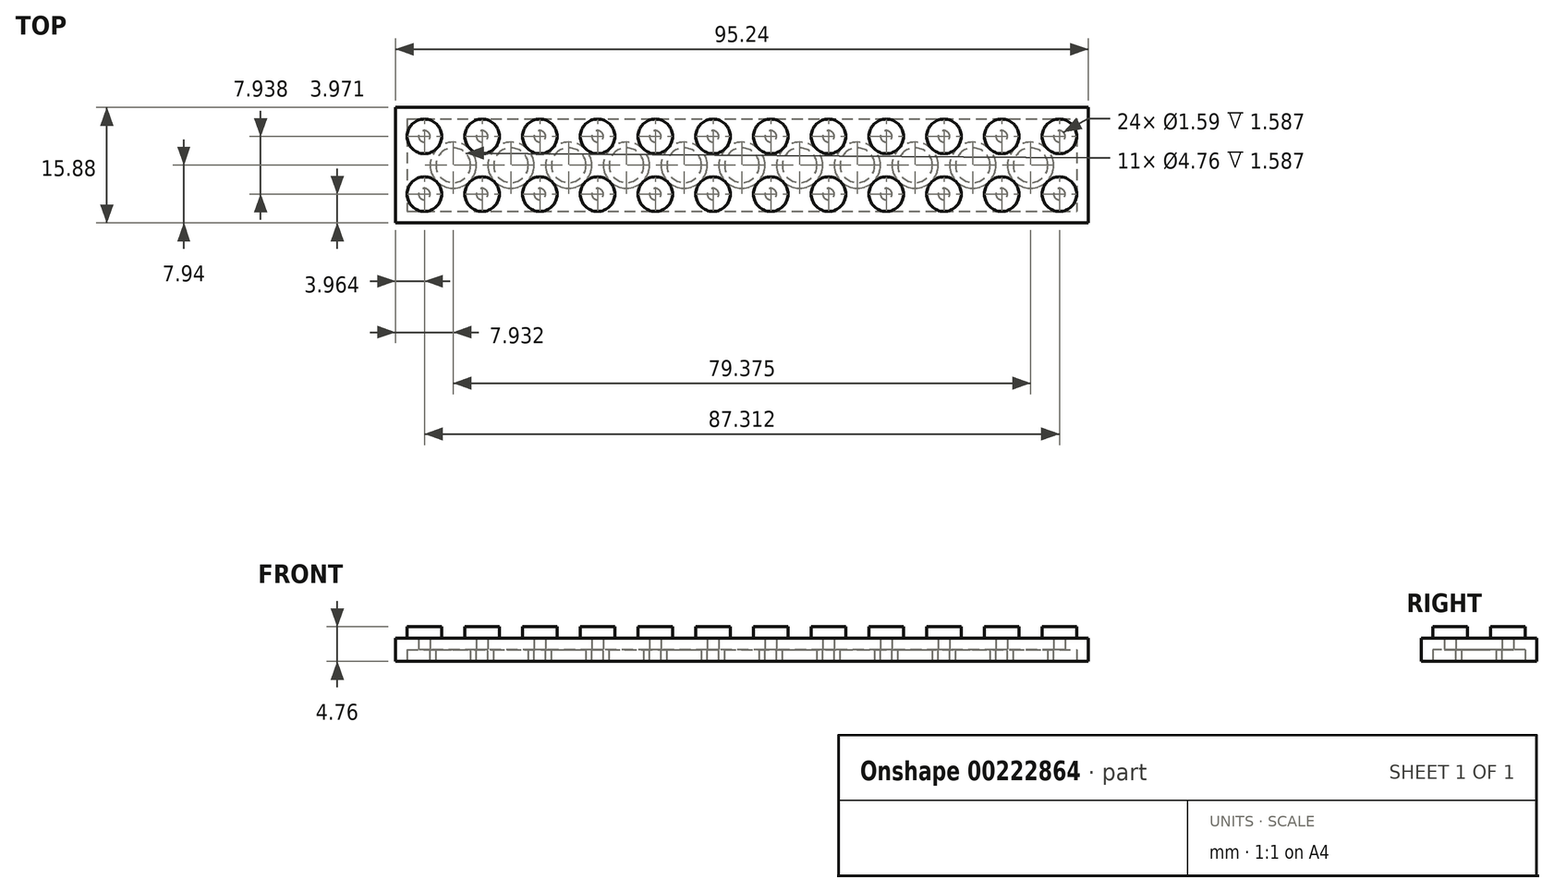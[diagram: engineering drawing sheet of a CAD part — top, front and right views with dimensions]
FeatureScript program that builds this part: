
annotation { "Feature Type Name" : "Feature", "Feature Type Description" : "" }
export const myFeature = defineFeature(function(context is Context, id is Id, definition is map)
    precondition{}
    {
        {
            var Q0;
            Q0=qCreatedBy(makeId("Top.planeOp"),FACE);
            var sketch = newSketch(context, id + "F0", { "sketchPlane" : qUnion([Q0])});
            skLineSegment(sketch, "E0.bottom", {"start": v(-47.63, 7.94) * mm, "end": v(47.63, 7.94) * mm});
            skLineSegment(sketch, "E0.top", {"start": v(-47.63, -7.94) * mm, "end": v(47.63, -7.94) * mm});
            skLineSegment(sketch, "E0.left", {"start": v(-47.63, 7.94) * mm, "end": v(-47.63, -7.94) * mm});
            skLineSegment(sketch, "E0.right", {"start": v(47.63, 7.94) * mm, "end": v(47.63, -7.94) * mm});
            skPoint(sketch, "E0.middle", {"position": v(0, 0) * mm});
            skCircle(sketch, "E1", {"center": v(-43.66, 3.97) * mm, "radius": 2.38 * mm});
            skCircle(sketch, "E2.0.1.0", {"center": v(-43.66, -3.97) * mm, "radius": 2.38 * mm});
            skCircle(sketch, "E2.1.0.0", {"center": v(-35.72, 3.97) * mm, "radius": 2.38 * mm});
            skCircle(sketch, "E2.1.1.0", {"center": v(-35.72, -3.97) * mm, "radius": 2.38 * mm});
            skCircle(sketch, "E2.2.0.0", {"center": v(-27.78, 3.97) * mm, "radius": 2.38 * mm});
            skCircle(sketch, "E2.2.1.0", {"center": v(-27.78, -3.97) * mm, "radius": 2.38 * mm});
            skCircle(sketch, "E2.3.0.0", {"center": v(-19.84, 3.97) * mm, "radius": 2.38 * mm});
            skCircle(sketch, "E2.3.1.0", {"center": v(-19.84, -3.97) * mm, "radius": 2.38 * mm});
            skCircle(sketch, "E2.4.0.0", {"center": v(-11.9, 3.97) * mm, "radius": 2.38 * mm});
            skCircle(sketch, "E2.4.1.0", {"center": v(-11.9, -3.97) * mm, "radius": 2.38 * mm});
            skCircle(sketch, "E2.5.0.0", {"center": v(-3.97, 3.97) * mm, "radius": 2.38 * mm});
            skCircle(sketch, "E2.5.1.0", {"center": v(-3.97, -3.97) * mm, "radius": 2.38 * mm});
            skCircle(sketch, "E2.6.0.0", {"center": v(3.97, 3.97) * mm, "radius": 2.38 * mm});
            skCircle(sketch, "E2.6.1.0", {"center": v(3.97, -3.97) * mm, "radius": 2.38 * mm});
            skCircle(sketch, "E2.7.0.0", {"center": v(11.9, 3.97) * mm, "radius": 2.38 * mm});
            skCircle(sketch, "E2.7.1.0", {"center": v(11.9, -3.97) * mm, "radius": 2.38 * mm});
            skCircle(sketch, "E2.8.0.0", {"center": v(19.84, 3.97) * mm, "radius": 2.38 * mm});
            skCircle(sketch, "E2.8.1.0", {"center": v(19.84, -3.97) * mm, "radius": 2.38 * mm});
            skCircle(sketch, "E2.9.0.0", {"center": v(27.78, 3.97) * mm, "radius": 2.38 * mm});
            skCircle(sketch, "E2.9.1.0", {"center": v(27.78, -3.97) * mm, "radius": 2.38 * mm});
            skCircle(sketch, "E2.10.0.0", {"center": v(35.72, 3.97) * mm, "radius": 2.38 * mm});
            skCircle(sketch, "E2.10.1.0", {"center": v(35.72, -3.97) * mm, "radius": 2.38 * mm});
            skCircle(sketch, "E2.11.0.0", {"center": v(43.66, 3.97) * mm, "radius": 2.38 * mm});
            skCircle(sketch, "E2.11.1.0", {"center": v(43.66, -3.97) * mm, "radius": 2.38 * mm});
            skLineSegment(sketch, "E2.direction1", {"start": v(-43.66, 3.97) * mm, "end": v(-35.72, 3.97) * mm, "construction": true});
            skLineSegment(sketch, "E2.direction2", {"start": v(-43.66, 3.97) * mm, "end": v(-43.66, -3.97) * mm, "construction": true});
            skSolve(sketch);
        }
        {
            var Q0;
            Q0=makeQuery(id+"F0.imprint","IMPRINT",FACE,{"disambiguationData":[TD([[makeQuery(id+"F0.imprint","IMPRINT",EDGE,{"derivedFrom":sQuery(id+"F0.wireOp",EDGE,"E0.bottom")}),-1.0]])]});
            extrude(context, id + "F1", {"entities" : qUnion([Q0]), "depth" : 3.17 * mm});
        }
        {
            var Q0;
            Q0=makeQuery(id+"F0.imprint","IMPRINT",FACE,{"disambiguationData":[TD([[makeQuery(id+"F0.imprint","IMPRINT",EDGE,{"derivedFrom":sQuery(id+"F0.wireOp",EDGE,"E1")}),1.0]])]});
            var Q1;
            Q1=makeQuery(id+"F0.imprint","IMPRINT",FACE,{"disambiguationData":[TD([[makeQuery(id+"F0.imprint","IMPRINT",EDGE,{"derivedFrom":sQuery(id+"F0.wireOp",EDGE,"E2.0.1.0")}),1.0]])]});
            var Q2;
            Q2=makeQuery(id+"F0.imprint","IMPRINT",FACE,{"disambiguationData":[TD([[makeQuery(id+"F0.imprint","IMPRINT",EDGE,{"derivedFrom":sQuery(id+"F0.wireOp",EDGE,"E2.1.1.0")}),1.0]])]});
            var Q3;
            Q3=makeQuery(id+"F0.imprint","IMPRINT",FACE,{"disambiguationData":[TD([[makeQuery(id+"F0.imprint","IMPRINT",EDGE,{"derivedFrom":sQuery(id+"F0.wireOp",EDGE,"E2.1.0.0")}),1.0]])]});
            var Q4;
            Q4=makeQuery(id+"F0.imprint","IMPRINT",FACE,{"disambiguationData":[TD([[makeQuery(id+"F0.imprint","IMPRINT",EDGE,{"derivedFrom":sQuery(id+"F0.wireOp",EDGE,"E2.2.0.0")}),1.0]])]});
            var Q5;
            Q5=makeQuery(id+"F0.imprint","IMPRINT",FACE,{"disambiguationData":[TD([[makeQuery(id+"F0.imprint","IMPRINT",EDGE,{"derivedFrom":sQuery(id+"F0.wireOp",EDGE,"E2.3.1.0")}),1.0]])]});
            var Q6;
            Q6=makeQuery(id+"F0.imprint","IMPRINT",FACE,{"disambiguationData":[TD([[makeQuery(id+"F0.imprint","IMPRINT",EDGE,{"derivedFrom":sQuery(id+"F0.wireOp",EDGE,"E2.3.0.0")}),1.0]])]});
            var Q7;
            Q7=makeQuery(id+"F0.imprint","IMPRINT",FACE,{"disambiguationData":[TD([[makeQuery(id+"F0.imprint","IMPRINT",EDGE,{"derivedFrom":sQuery(id+"F0.wireOp",EDGE,"E2.4.0.0")}),1.0]])]});
            var Q8;
            Q8=makeQuery(id+"F0.imprint","IMPRINT",FACE,{"disambiguationData":[TD([[makeQuery(id+"F0.imprint","IMPRINT",EDGE,{"derivedFrom":sQuery(id+"F0.wireOp",EDGE,"E2.4.1.0")}),1.0]])]});
            var Q9;
            Q9=makeQuery(id+"F0.imprint","IMPRINT",FACE,{"disambiguationData":[TD([[makeQuery(id+"F0.imprint","IMPRINT",EDGE,{"derivedFrom":sQuery(id+"F0.wireOp",EDGE,"E2.2.1.0")}),1.0]])]});
            var Q10;
            Q10=makeQuery(id+"F0.imprint","IMPRINT",FACE,{"disambiguationData":[TD([[makeQuery(id+"F0.imprint","IMPRINT",EDGE,{"derivedFrom":sQuery(id+"F0.wireOp",EDGE,"E2.5.1.0")}),1.0]])]});
            var Q11;
            Q11=makeQuery(id+"F0.imprint","IMPRINT",FACE,{"disambiguationData":[TD([[makeQuery(id+"F0.imprint","IMPRINT",EDGE,{"derivedFrom":sQuery(id+"F0.wireOp",EDGE,"E2.5.0.0")}),1.0]])]});
            var Q12;
            Q12=makeQuery(id+"F0.imprint","IMPRINT",FACE,{"disambiguationData":[TD([[makeQuery(id+"F0.imprint","IMPRINT",EDGE,{"derivedFrom":sQuery(id+"F0.wireOp",EDGE,"E2.6.0.0")}),1.0]])]});
            var Q13;
            Q13=makeQuery(id+"F0.imprint","IMPRINT",FACE,{"disambiguationData":[TD([[makeQuery(id+"F0.imprint","IMPRINT",EDGE,{"derivedFrom":sQuery(id+"F0.wireOp",EDGE,"E2.6.1.0")}),1.0]])]});
            var Q14;
            Q14=makeQuery(id+"F0.imprint","IMPRINT",FACE,{"disambiguationData":[TD([[makeQuery(id+"F0.imprint","IMPRINT",EDGE,{"derivedFrom":sQuery(id+"F0.wireOp",EDGE,"E2.7.1.0")}),1.0]])]});
            var Q15;
            Q15=makeQuery(id+"F0.imprint","IMPRINT",FACE,{"disambiguationData":[TD([[makeQuery(id+"F0.imprint","IMPRINT",EDGE,{"derivedFrom":sQuery(id+"F0.wireOp",EDGE,"E2.7.0.0")}),1.0]])]});
            var Q16;
            Q16=makeQuery(id+"F0.imprint","IMPRINT",FACE,{"disambiguationData":[TD([[makeQuery(id+"F0.imprint","IMPRINT",EDGE,{"derivedFrom":sQuery(id+"F0.wireOp",EDGE,"E2.8.0.0")}),1.0]])]});
            var Q17;
            Q17=makeQuery(id+"F0.imprint","IMPRINT",FACE,{"disambiguationData":[TD([[makeQuery(id+"F0.imprint","IMPRINT",EDGE,{"derivedFrom":sQuery(id+"F0.wireOp",EDGE,"E2.8.1.0")}),1.0]])]});
            var Q18;
            Q18=makeQuery(id+"F0.imprint","IMPRINT",FACE,{"disambiguationData":[TD([[makeQuery(id+"F0.imprint","IMPRINT",EDGE,{"derivedFrom":sQuery(id+"F0.wireOp",EDGE,"E2.9.1.0")}),1.0]])]});
            var Q19;
            Q19=makeQuery(id+"F0.imprint","IMPRINT",FACE,{"disambiguationData":[TD([[makeQuery(id+"F0.imprint","IMPRINT",EDGE,{"derivedFrom":sQuery(id+"F0.wireOp",EDGE,"E2.9.0.0")}),1.0]])]});
            var Q20;
            Q20=makeQuery(id+"F0.imprint","IMPRINT",FACE,{"disambiguationData":[TD([[makeQuery(id+"F0.imprint","IMPRINT",EDGE,{"derivedFrom":sQuery(id+"F0.wireOp",EDGE,"E2.10.0.0")}),1.0]])]});
            var Q21;
            Q21=makeQuery(id+"F0.imprint","IMPRINT",FACE,{"disambiguationData":[TD([[makeQuery(id+"F0.imprint","IMPRINT",EDGE,{"derivedFrom":sQuery(id+"F0.wireOp",EDGE,"E2.10.1.0")}),1.0]])]});
            var Q22;
            Q22=makeQuery(id+"F0.imprint","IMPRINT",FACE,{"disambiguationData":[TD([[makeQuery(id+"F0.imprint","IMPRINT",EDGE,{"derivedFrom":sQuery(id+"F0.wireOp",EDGE,"E2.11.0.0")}),1.0]])]});
            var Q23;
            Q23=makeQuery(id+"F0.imprint","IMPRINT",FACE,{"disambiguationData":[TD([[makeQuery(id+"F0.imprint","IMPRINT",EDGE,{"derivedFrom":sQuery(id+"F0.wireOp",EDGE,"E2.11.1.0")}),1.0]])]});
            extrude(context, id + "F2", {"entities" : qUnion([Q0, Q1, Q2, Q3, Q4, Q5, Q6, Q7, Q8, Q9, Q10, Q11, Q12, Q13, Q14, Q15, Q16, Q17, Q18, Q19, Q20, Q21, Q22, Q23]), "operationType" : NewBodyOperationType.ADD, "depth" : 4.76 * mm});
        }
        {
            var Q0;
            {var subQ0=sQuery(id+"F0.wireOp",EDGE,"8b71ed98-f0e1-4300-85cb-82ad82c44b3e0.MirrorC");var subQ1=sQuery(id+"F0.wireOp",EDGE,"k7z4QqMS-RwRw-DD0v-TLlN-AgkNKQtf4ZrW");Q0=makeQuery(id+"F2.boolean.opBoolean","MERGE",FACE,{"derivedFrom":[makeQuery(id+"F1.opExtrude","CAP_FACE",FACE,{"disambiguationData":[OSD([sQuery(id+"F0.wireOp",EDGE,"E0.bottom"),sQuery(id+"F0.wireOp",EDGE,"E0.top"),sQuery(id+"F0.wireOp",EDGE,"E0.left"),sQuery(id+"F0.wireOp",EDGE,"E0.right"),subQ1,subQ0])],"isStart":true}),makeQuery(id+"F2.opExtrude","CAP_FACE",FACE,{"disambiguationData":[OSD([subQ1])],"isStart":true}),makeQuery(id+"F2.opExtrude","CAP_FACE",FACE,{"disambiguationData":[OSD([subQ0])],"isStart":true})]});}
            shell(context, id + "F3", {"entities" : qUnion([Q0]), "thickness" : 1.59 * mm});
        }
        {
            var Q0;
            Q0=makeQuery(id+"F3.opShell","OFFSET_FACE",FACE,{"disambiguationData":[OSD([sQuery(id+"F0.wireOp",EDGE,"E0.bottom"),sQuery(id+"F0.wireOp",EDGE,"E0.top"),sQuery(id+"F0.wireOp",EDGE,"E0.left"),sQuery(id+"F0.wireOp",EDGE,"E0.right"),sQuery(id+"F0.wireOp",EDGE,"E1"),sQuery(id+"F0.wireOp",EDGE,"E2.0.1.0"),sQuery(id+"F0.wireOp",EDGE,"E2.1.0.0"),sQuery(id+"F0.wireOp",EDGE,"E2.1.1.0"),sQuery(id+"F0.wireOp",EDGE,"E2.2.0.0"),sQuery(id+"F0.wireOp",EDGE,"E2.2.1.0"),sQuery(id+"F0.wireOp",EDGE,"E2.3.0.0"),sQuery(id+"F0.wireOp",EDGE,"E2.3.1.0"),sQuery(id+"F0.wireOp",EDGE,"E2.4.0.0"),sQuery(id+"F0.wireOp",EDGE,"E2.4.1.0"),sQuery(id+"F0.wireOp",EDGE,"E2.5.0.0"),sQuery(id+"F0.wireOp",EDGE,"E2.5.1.0"),sQuery(id+"F0.wireOp",EDGE,"E2.6.0.0"),sQuery(id+"F0.wireOp",EDGE,"E2.6.1.0"),sQuery(id+"F0.wireOp",EDGE,"E2.7.0.0"),sQuery(id+"F0.wireOp",EDGE,"E2.7.1.0"),sQuery(id+"F0.wireOp",EDGE,"E2.8.0.0"),sQuery(id+"F0.wireOp",EDGE,"E2.8.1.0"),sQuery(id+"F0.wireOp",EDGE,"E2.9.0.0"),sQuery(id+"F0.wireOp",EDGE,"E2.9.1.0"),sQuery(id+"F0.wireOp",EDGE,"E2.10.0.0"),sQuery(id+"F0.wireOp",EDGE,"E2.10.1.0"),sQuery(id+"F0.wireOp",EDGE,"E2.11.0.0"),sQuery(id+"F0.wireOp",EDGE,"E2.11.1.0")])]});
            var sketch = newSketch(context, id + "F4", { "sketchPlane" : qUnion([Q0])});
            skCircle(sketch, "E3.1.0.0", {"center": v(-39.69, 0) * mm, "radius": 3.18 * mm});
            skCircle(sketch, "E3.1.0.1", {"center": v(-39.69, 0) * mm, "radius": 2.38 * mm});
            skCircle(sketch, "E4.1.0.0", {"center": v(-31.75, 0) * mm, "radius": 3.18 * mm});
            skCircle(sketch, "E4.1.0.1", {"center": v(-31.75, 0) * mm, "radius": 2.38 * mm});
            skCircle(sketch, "E4.2.0.0", {"center": v(-23.81, 0) * mm, "radius": 3.18 * mm});
            skCircle(sketch, "E4.2.0.1", {"center": v(-23.81, 0) * mm, "radius": 2.38 * mm});
            skCircle(sketch, "E4.3.0.0", {"center": v(-15.88, 0) * mm, "radius": 3.18 * mm});
            skCircle(sketch, "E4.3.0.1", {"center": v(-15.88, 0) * mm, "radius": 2.38 * mm});
            skCircle(sketch, "E4.4.0.0", {"center": v(-7.94, 0) * mm, "radius": 3.18 * mm});
            skCircle(sketch, "E4.4.0.1", {"center": v(-7.94, 0) * mm, "radius": 2.38 * mm});
            skCircle(sketch, "E4.5.0.0", {"center": v(0, 0) * mm, "radius": 3.18 * mm});
            skCircle(sketch, "E4.5.0.1", {"center": v(0, 0) * mm, "radius": 2.38 * mm});
            skCircle(sketch, "E4.6.0.0", {"center": v(7.94, 0) * mm, "radius": 3.18 * mm});
            skCircle(sketch, "E4.6.0.1", {"center": v(7.94, 0) * mm, "radius": 2.38 * mm});
            skLineSegment(sketch, "E4.direction1", {"start": v(-39.69, 0) * mm, "end": v(-31.75, 0) * mm, "construction": true});
            skCircle(sketch, "E5.0.7.0", {"center": v(15.87, 0) * mm, "radius": 3.18 * mm});
            skCircle(sketch, "E5.2.7.0", {"center": v(15.87, 0) * mm, "radius": 2.38 * mm});
            skCircle(sketch, "E5.0.8.0", {"center": v(23.81, 0) * mm, "radius": 3.18 * mm});
            skCircle(sketch, "E5.2.8.0", {"center": v(23.81, 0) * mm, "radius": 2.38 * mm});
            skCircle(sketch, "E5.0.9.0", {"center": v(31.75, 0) * mm, "radius": 3.18 * mm});
            skCircle(sketch, "E5.2.9.0", {"center": v(31.75, 0) * mm, "radius": 2.38 * mm});
            skCircle(sketch, "E5.0.10.0", {"center": v(39.69, 0) * mm, "radius": 3.18 * mm});
            skCircle(sketch, "E5.2.10.0", {"center": v(39.69, 0) * mm, "radius": 2.38 * mm});
            skSolve(sketch);
        }
        {
            var Q0;
            Q0=makeQuery(id+"F4.imprint","IMPRINT",FACE,{"disambiguationData":[TD([[makeQuery(id+"F4.imprint","IMPRINT",EDGE,{"derivedFrom":sQuery(id+"F4.wireOp",EDGE,"E3.1.0.0")}),1.0]])]});
            var Q1;
            Q1=makeQuery(id+"F4.imprint","IMPRINT",FACE,{"disambiguationData":[TD([[makeQuery(id+"F4.imprint","IMPRINT",EDGE,{"derivedFrom":sQuery(id+"F4.wireOp",EDGE,"E4.1.0.0")}),1.0]])]});
            var Q2;
            Q2=makeQuery(id+"F4.imprint","IMPRINT",FACE,{"disambiguationData":[TD([[makeQuery(id+"F4.imprint","IMPRINT",EDGE,{"derivedFrom":sQuery(id+"F4.wireOp",EDGE,"E4.2.0.0")}),1.0]])]});
            var Q3;
            Q3=makeQuery(id+"F4.imprint","IMPRINT",FACE,{"disambiguationData":[TD([[makeQuery(id+"F4.imprint","IMPRINT",EDGE,{"derivedFrom":sQuery(id+"F4.wireOp",EDGE,"E4.3.0.0")}),1.0]])]});
            var Q4;
            Q4=makeQuery(id+"F4.imprint","IMPRINT",FACE,{"disambiguationData":[TD([[makeQuery(id+"F4.imprint","IMPRINT",EDGE,{"derivedFrom":sQuery(id+"F4.wireOp",EDGE,"E4.4.0.0")}),1.0]])]});
            var Q5;
            Q5=makeQuery(id+"F4.imprint","IMPRINT",FACE,{"disambiguationData":[TD([[makeQuery(id+"F4.imprint","IMPRINT",EDGE,{"derivedFrom":sQuery(id+"F4.wireOp",EDGE,"E4.5.0.0")}),1.0]])]});
            var Q6;
            Q6=makeQuery(id+"F4.imprint","IMPRINT",FACE,{"disambiguationData":[TD([[makeQuery(id+"F4.imprint","IMPRINT",EDGE,{"derivedFrom":sQuery(id+"F4.wireOp",EDGE,"E4.6.0.0")}),1.0]])]});
            var Q7;
            Q7=makeQuery(id+"F4.imprint","IMPRINT",FACE,{"disambiguationData":[TD([[makeQuery(id+"F4.imprint","IMPRINT",EDGE,{"derivedFrom":sQuery(id+"F4.wireOp",EDGE,"E5.0.7.0")}),1.0]])]});
            var Q8;
            Q8=makeQuery(id+"F4.imprint","IMPRINT",FACE,{"disambiguationData":[TD([[makeQuery(id+"F4.imprint","IMPRINT",EDGE,{"derivedFrom":sQuery(id+"F4.wireOp",EDGE,"E5.0.8.0")}),1.0]])]});
            var Q9;
            Q9=makeQuery(id+"F4.imprint","IMPRINT",FACE,{"disambiguationData":[TD([[makeQuery(id+"F4.imprint","IMPRINT",EDGE,{"derivedFrom":sQuery(id+"F4.wireOp",EDGE,"E5.0.9.0")}),1.0]])]});
            var Q10;
            Q10=makeQuery(id+"F4.imprint","IMPRINT",FACE,{"disambiguationData":[TD([[makeQuery(id+"F4.imprint","IMPRINT",EDGE,{"derivedFrom":sQuery(id+"F4.wireOp",EDGE,"E5.0.10.0")}),1.0]])]});
            extrude(context, id + "F5", {"entities" : qUnion([Q0, Q1, Q2, Q3, Q4, Q5, Q6, Q7, Q8, Q9, Q10]), "operationType" : NewBodyOperationType.ADD, "depth" : 1.59 * mm});
        }
    });
